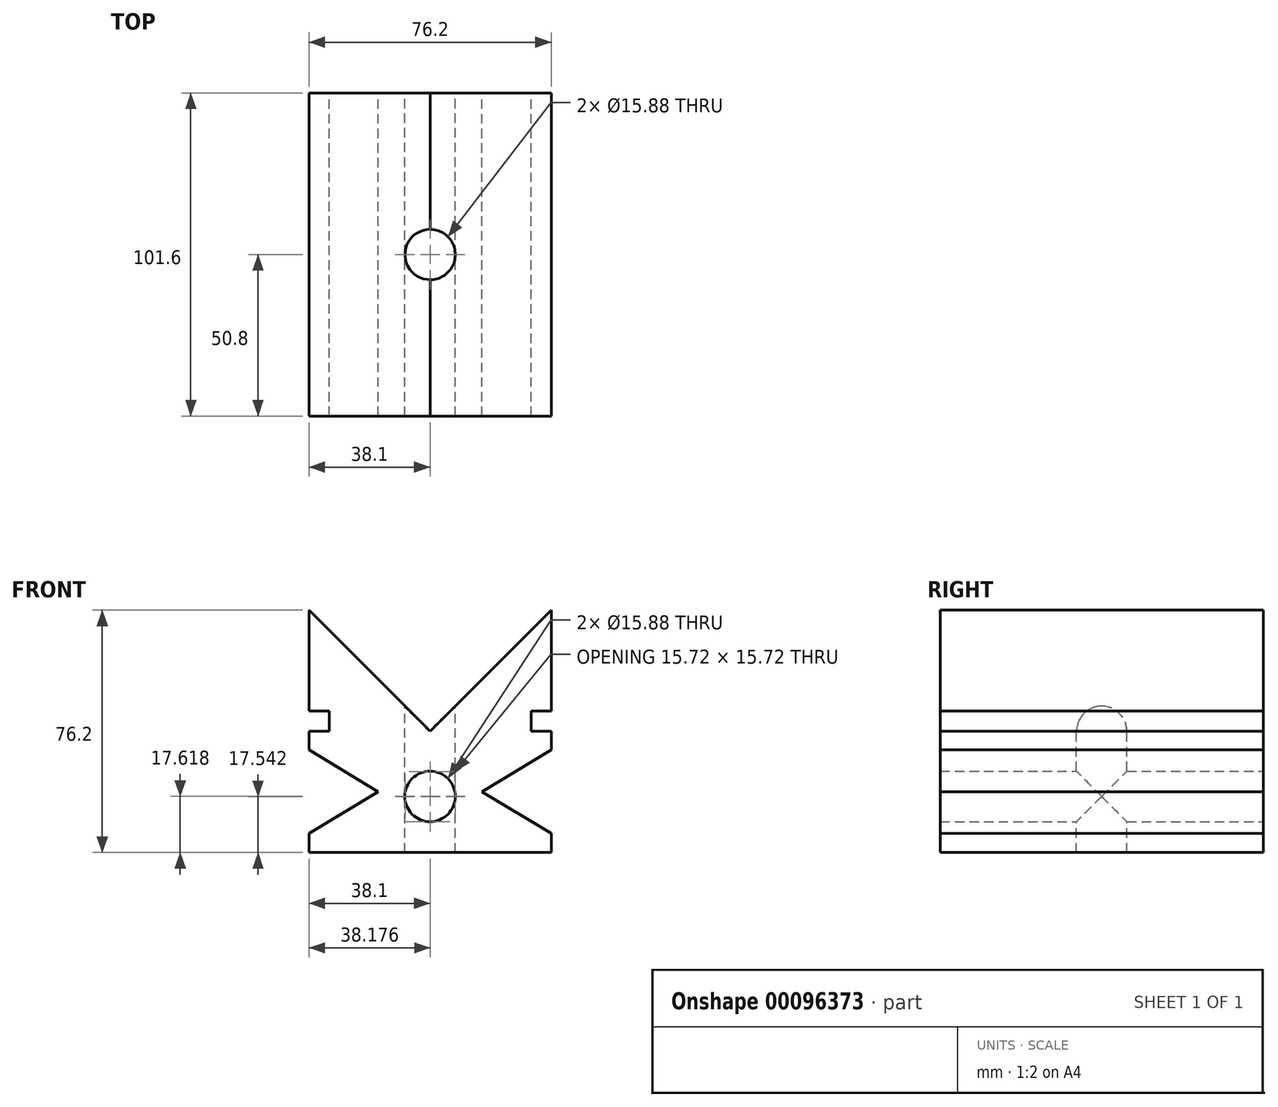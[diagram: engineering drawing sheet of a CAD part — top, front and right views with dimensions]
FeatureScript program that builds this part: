
annotation { "Feature Type Name" : "Feature", "Feature Type Description" : "" }
export const myFeature = defineFeature(function(context is Context, id is Id, definition is map)
    precondition{}
    {
        {
            var Q0;
            Q0=qCreatedBy(makeId("Front.planeOp"),FACE);
            var sketch = newSketch(context, id + "F0", { "sketchPlane" : qUnion([Q0])});
            skLineSegment(sketch, "E0.top", {"start": v(-38.1, -38.1) * mm, "end": v(38.1, -38.1) * mm});
            skLineSegment(sketch, "E0.left", {"start": v(-38.1, 38.1) * mm, "end": v(-38.1, -38.1) * mm});
            skLineSegment(sketch, "E0.right", {"start": v(38.1, 38.1) * mm, "end": v(38.1, -38.1) * mm});
            skPoint(sketch, "E0.middle", {"position": v(0, 0) * mm});
            skLineSegment(sketch, "E1", {"start": v(-38.1, 38.1) * mm, "end": v(0, 0) * mm});
            skLineSegment(sketch, "E2", {"start": v(38.1, 38.1) * mm, "end": v(0, 0) * mm});
            skLineSegment(sketch, "E3.bottom", {"start": v(-38.1, 0) * mm, "end": v(-31.75, 0) * mm});
            skLineSegment(sketch, "E3.top", {"start": v(-38.1, 6.35) * mm, "end": v(-31.75, 6.35) * mm});
            skLineSegment(sketch, "E3.right", {"start": v(-31.75, 0) * mm, "end": v(-31.75, 6.35) * mm});
            skLineSegment(sketch, "E4.MirrorCS", {"start": v(31.75, 0) * mm, "end": v(31.75, 6.35) * mm});
            skLineSegment(sketch, "E5.MirrorCS", {"start": v(38.1, 6.35) * mm, "end": v(31.75, 6.35) * mm});
            skLineSegment(sketch, "E6.MirrorCS", {"start": v(38.1, 0) * mm, "end": v(31.75, 0) * mm});
            skLineSegment(sketch, "E7", {"start": v(-38.1, -5.88) * mm, "end": v(-16.36, -19.01) * mm});
            skLineSegment(sketch, "E8", {"start": v(-16.36, -19.01) * mm, "end": v(-38.1, -32.14) * mm});
            skLineSegment(sketch, "E9.MirrorCS", {"start": v(38.1, -5.88) * mm, "end": v(16.36, -19.01) * mm});
            skLineSegment(sketch, "E10.MirrorCS", {"start": v(16.36, -19.01) * mm, "end": v(38.1, -32.14) * mm});
            skCircle(sketch, "E11", {"center": v(0, -20.48) * mm, "radius": 7.94 * mm});
            skSolve(sketch);
        }
        {
            var Q0;
            {var subQ7=sQuery(id+"F0.wireOp",EDGE,"E0.top");Q0=makeQuery(id+"F0.imprint","IMPRINT",FACE,{"disambiguationData":[TD([[makeQuery(id+"F0.imprint","IMPRINT",EDGE,{"derivedFrom":subQ7}),1.0]])]});}
            extrude(context, id + "F1", {"entities" : qUnion([Q0]), "endBound" : BoundingType.SYMMETRIC, "depth" : 101.6 * mm});
        }
        {
            var Q0;
            Q0=qCreatedBy(makeId("Top.planeOp"),FACE);
            var sketch = newSketch(context, id + "F2", { "sketchPlane" : qUnion([Q0])});
            skCircle(sketch, "E12", {"center": v(0, 0) * mm, "radius": 7.94 * mm});
            skSolve(sketch);
        }
        {
            var Q0;
            Q0 = qSketchRegion(id + "F2", true);
            extrude(context, id + "F3", {"entities" : qUnion([Q0]), "operationType" : NewBodyOperationType.REMOVE, "endBound" : BoundingType.SYMMETRIC, "oppositeDirection" : true, "depth" : 101.6 * mm});
        }
    });
